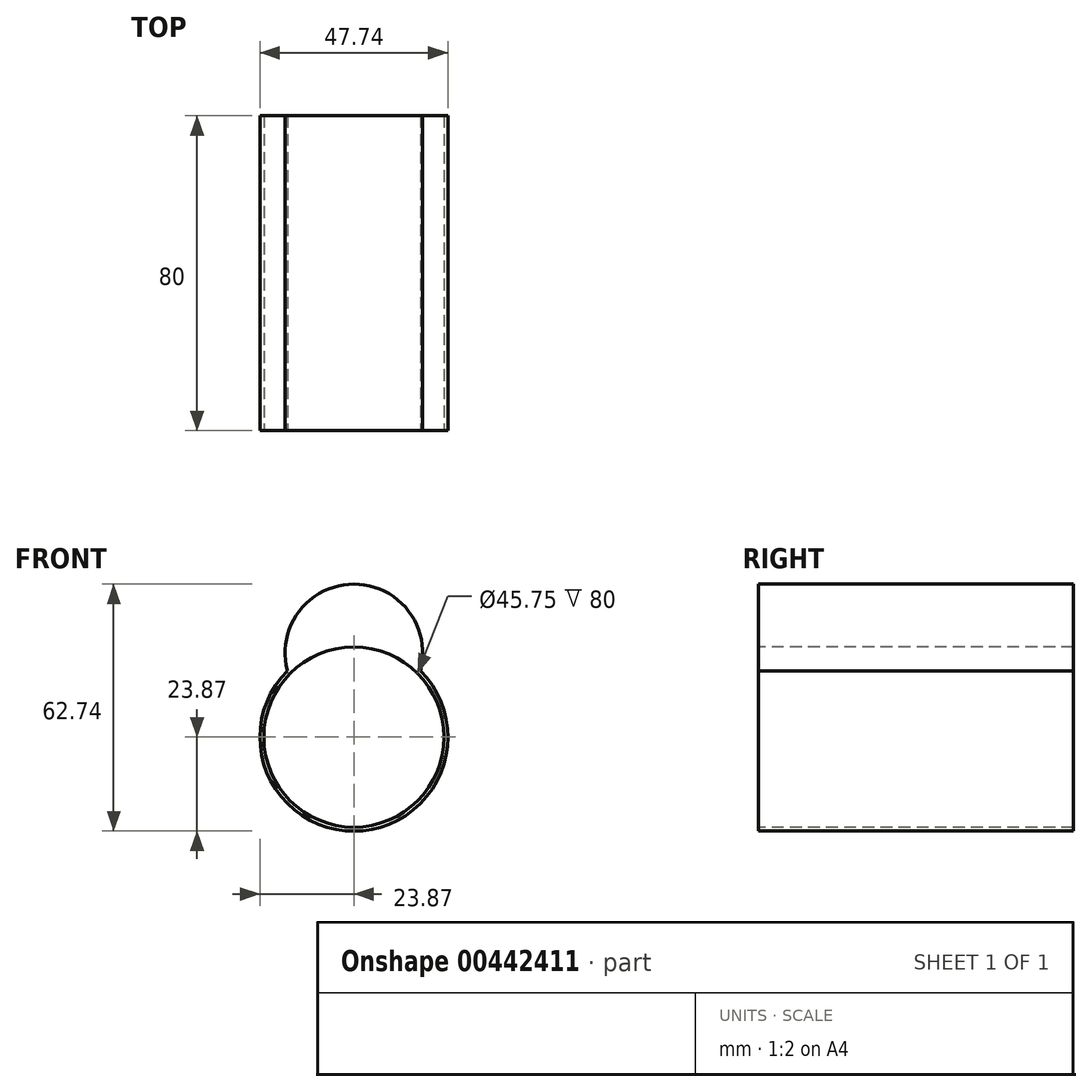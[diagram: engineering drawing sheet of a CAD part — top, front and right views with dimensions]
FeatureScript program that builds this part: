
annotation { "Feature Type Name" : "Feature", "Feature Type Description" : "" }
export const myFeature = defineFeature(function(context is Context, id is Id, definition is map)
    precondition{}
    {
        {
            var Q0;
            Q0=qCreatedBy(makeId("Front.planeOp"),FACE);
            var sketch = newSketch(context, id + "F0", { "sketchPlane" : qUnion([Q0])});
            skCircle(sketch, "E0", {"center": v(0, 0) * mm, "radius": 23.87 * mm});
            skSolve(sketch);
        }
        {
            var Q0;
            Q0=makeQuery(id+"F0.imprint","IMPRINT",FACE,{"disambiguationData":[TD([[makeQuery(id+"F0.imprint","IMPRINT",EDGE,{"derivedFrom":sQuery(id+"F0.wireOp",EDGE,"E0")}),1.0]])]});
            extrude(context, id + "F1", {"entities" : qUnion([Q0]), "oppositeDirection" : true, "depth" : 80 * mm});
        }
        {
            var Q0;
            Q0=makeQuery(id+"F1.opExtrude","CAP_FACE",FACE,{"disambiguationData":[OSD([sQuery(id+"F0.wireOp",EDGE,"E0")])],"isStart":true});
            var sketch = newSketch(context, id + "F2", { "sketchPlane" : qUnion([Q0])});
            skCircle(sketch, "E1", {"center": v(0, 0) * mm, "radius": 22.87 * mm});
            skSolve(sketch);
        }
        {
            var Q0;
            Q0=makeQuery(id+"F2.imprint","IMPRINT",FACE,{"disambiguationData":[TD([[makeQuery(id+"F2.imprint","IMPRINT",EDGE,{"derivedFrom":sQuery(id+"F2.wireOp",EDGE,"E1")}),1.0]])]});
            extrude(context, id + "F3", {"entities" : qUnion([Q0]), "operationType" : NewBodyOperationType.REMOVE, "oppositeDirection" : true, "depth" : 80 * mm});
        }
        {
            var Q0;
            Q0=makeQuery(id+"F1.opExtrude","CAP_FACE",FACE,{"disambiguationData":[OSD([sQuery(id+"F0.wireOp",EDGE,"E0")])],"isStart":true});
            var sketch = newSketch(context, id + "F4", { "sketchPlane" : qUnion([Q0])});
            skArc(sketch, "E2", {"start": v(16.89, 16.87) * mm, "mid": v(0, 23.87) * mm, "end": v(-16.87, 16.89) * mm});
            skPoint(sketch, "E2.startSnap0", {"position": v(-16.87, 16.87) * mm});
            skPoint(sketch, "E2.endSnap0", {"position": v(-16.87, 16.87) * mm});
            skArc(sketch, "E3", {"start": v(16.89, 16.87) * mm, "mid": v(0.02, 38.87) * mm, "end": v(-16.87, 16.89) * mm});
            skSolve(sketch);
        }
        {
            var Q0;
            Q0=makeQuery(id+"F4.imprint","IMPRINT",FACE,{"disambiguationData":[TD([[makeQuery(id+"F4.imprint","IMPRINT",EDGE,{"derivedFrom":sQuery(id+"F4.wireOp",EDGE,"E2")}),-1.0]])]});
            extrude(context, id + "F5", {"entities" : qUnion([Q0]), "operationType" : NewBodyOperationType.ADD, "oppositeDirection" : true, "depth" : 80 * mm});
        }
    });
